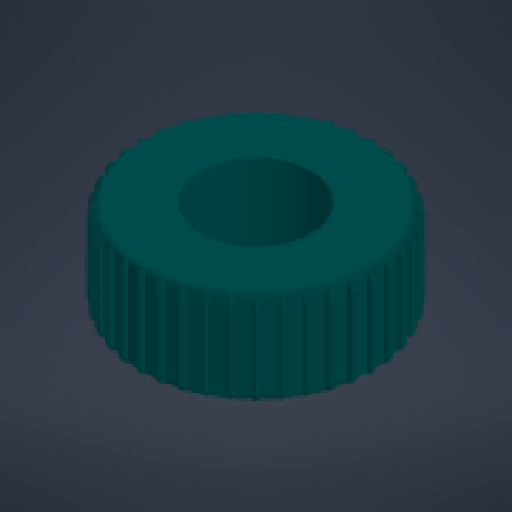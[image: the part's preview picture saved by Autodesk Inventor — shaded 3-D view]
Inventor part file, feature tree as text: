
AUTODESK INVENTOR PART (.ipt)
format: ipt  version: 2024 (Build 280153000, 153)  size: 1,047,040 bytes
history: native  units: mm
features: extrude x2, fillet x2, sketch x2, other x1, chamfer x1, pattern_circular x1
ambient origin geometry x8: Origin, YZ Plane, XZ Plane, XY Plane, X Axis, Y Axis, Z Axis, Center Point
bodies: Body1 (feature_tree)
feature tree (9):
  other  "Твердое тело1"
  extrude  "Выдавливание1"  Depth=60.0mm
  extrude  "Выдавливание2"  Depth=125.0mm
  fillet  "Сопряжение2"  Radius=51.0mm
  chamfer  "Фаска1"  Distance=3.0mm
  pattern_circular  "Круговой массив1"  [2 undecoded]
  fillet  "Сопряжение3"  [1 undecoded]
  sketch  "Эскиз1"
  sketch  "Эскиз3"
note: 3 required parameter values undecoded (feature->parameter linkage not recoverable at this tier; creation-order binding heuristic only, values carry confidence <= 0.55)
